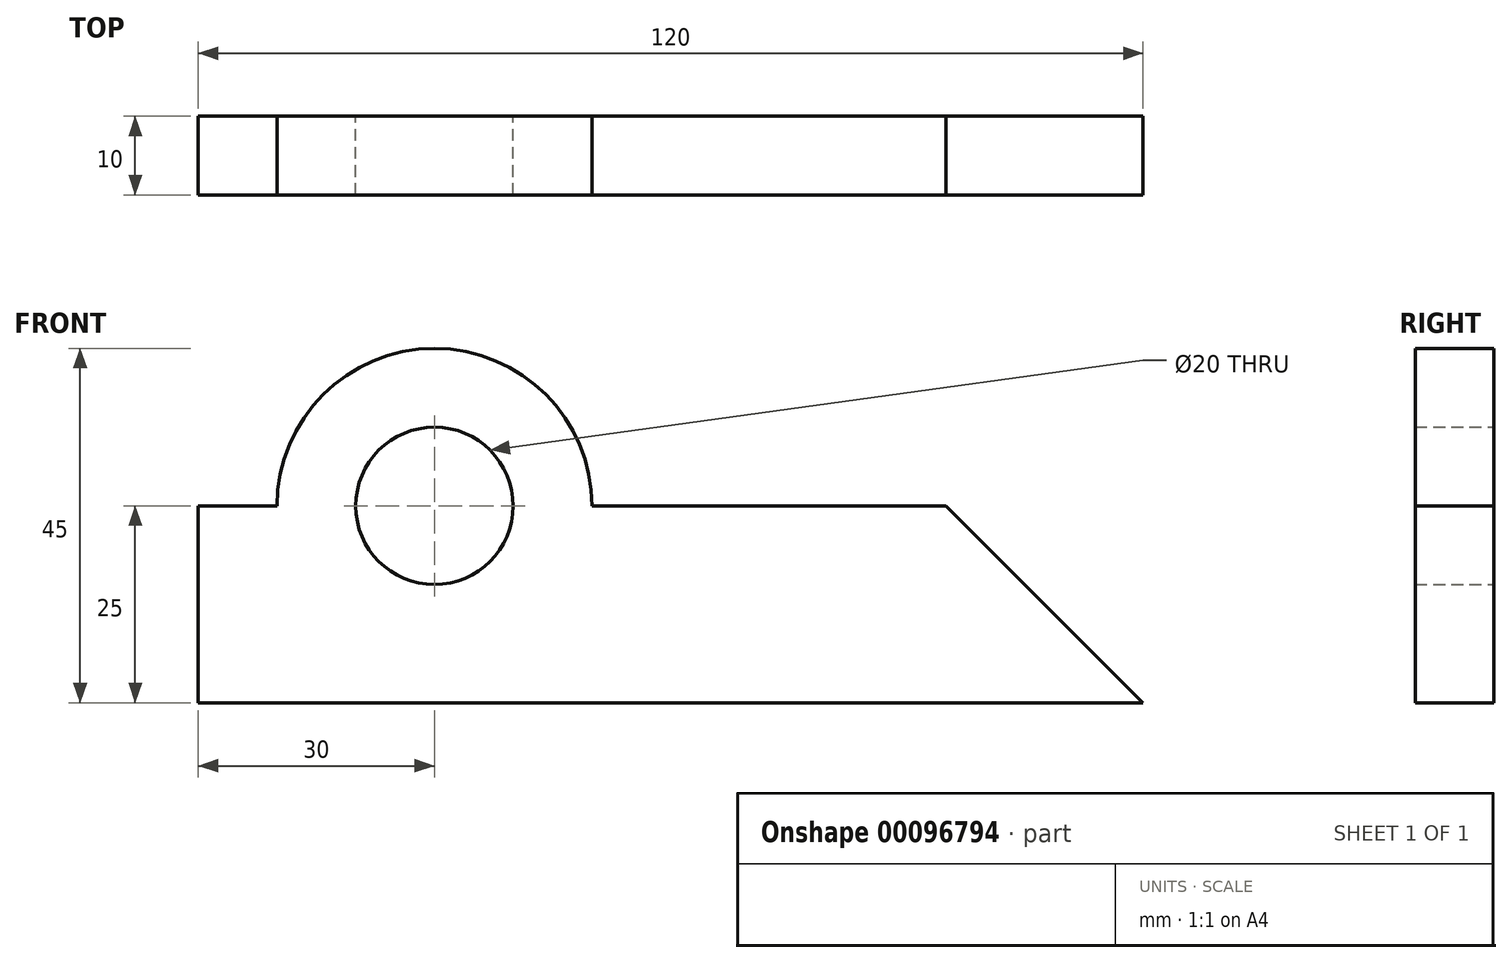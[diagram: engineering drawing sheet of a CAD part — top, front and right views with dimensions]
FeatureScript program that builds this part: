
annotation { "Feature Type Name" : "Feature", "Feature Type Description" : "" }
export const myFeature = defineFeature(function(context is Context, id is Id, definition is map)
    precondition{}
    {
        {
            var Q0;
            Q0=qCreatedBy(makeId("Front.planeOp"),FACE);
            var sketch = newSketch(context, id + "F0", { "sketchPlane" : qUnion([Q0])});
            skLineSegment(sketch, "E0", {"start": v(0, 0) * mm, "end": v(0, 25) * mm});
            skLineSegment(sketch, "E1", {"start": v(0, 25) * mm, "end": v(10, 25) * mm});
            skLineSegment(sketch, "E2", {"start": v(0, 0) * mm, "end": v(120, 0) * mm});
            skLineSegment(sketch, "E3", {"start": v(120, 0) * mm, "end": v(95, 25) * mm});
            skLineSegment(sketch, "E4", {"start": v(95, 25) * mm, "end": v(49.85, 25) * mm});
            skLineSegment(sketch, "E5", {"start": v(30, 45) * mm, "end": v(30, 0) * mm, "construction": true});
            skLineSegment(sketch, "E6", {"start": v(10, 25) * mm, "end": v(49.85, 25) * mm, "construction": true});
            skCircle(sketch, "E7", {"center": v(30, 25) * mm, "radius": 10 * mm});
            skArc(sketch, "E8", {"start": v(10, 25) * mm, "mid": v(30, 45) * mm, "end": v(50, 25) * mm});
            skSolve(sketch);
        }
        {
            var Q0;
            Q0 = qSketchRegion(id + "F0", true);
            extrude(context, id + "F1", {"entities" : qUnion([Q0]), "depth" : 10 * mm});
        }
    });
